# Revit family: Haworth_ComposeStorage_StorageUnit
name_source: partatom
category: Furniture Systems
revit_build: Autodesk Revit 2018 (Build: 20170223_1515(x64)
units: mm (PartAtom-declared; Revit-internal decimal feet)

## family parameters
Always vertical = Yes
Cut with Voids When Loaded = No
OmniClass Number = 23.40.70.14.64.21
OmniClass Title = Systems Furniture
Part Type = Normal
Room Calculation Point = No
Round Connector Dimension = Use Diameter
Shared = No
Work Plane-Based = No

## types (24) — shared parameters
Assembly Code = E2020200
Back Finish = Haworth _ Wood _ White Oak
Base = Yes
Base Finish = Haworth _ Wood _ White Oak
Base Height = 1"
Cabinet Finish = Haworth _ Wood _ White Oak
Chamfer Legs = No
Custom Size = No
Description = Haworth - Compose - Storage Unit
Door Finish = Haworth _ Wood _ White Oak
Finished Back = No
Manufacturer = Haworth
Max. Depth = 22"
Max. Height = 55"
Max. Width = 36"
Min. Depth = 16"
Min. Height = 19"
Min. Width = 30"
Model = BZS
Plynth Base = No
Revision Number = 4
Side Panel Base = Yes
Size = Verify Final Dim. w/ Haworth
Spacer Finish = Haworth _ Wood _ White Oak
Spacer Height = 0"
Standard Depths = 16, 22 in.
Standard Height = 14 1/4, 26 1/4, 38 1/4 in.
Standard Widths = 30, 36 in.
Sustainability Info = http://media.haworth.com
Top Spacer = No
URL = www.haworth.com
URL - Product = http://www.haworth.com
Warranty = http://www.haworth.com

## per-type parameters (varying)
| type | Actual Depth | Actual Height | Actual Width | Depth | Depth Adjuster | Door Height | Door Width | Doors | One High | Shelf 1 | Shelf 1 Offset | Shelf 2 | Shelf 2 Offet | Three High | Two High | Width |
| 1 High 30w 16d - No Doors | 16" | 14 1/4" | 30" | 16" | 0" | 13 1/4" | 15" | No | Yes | No | 4 43/256" | No | 4 43/256" | No | No | 30" |
| 1 High 30w 22d - No Doors | 22" | 14 1/4" | 30" | 22" | 0" | 13 1/4" | 15" | No | Yes | No | 4 43/256" | No | 4 43/256" | No | No | 30" |
| 1 High 36w 16d - No Doors | 16" | 14 1/4" | 36" | 16" | 0" | 13 1/4" | 18" | No | Yes | No | 4 43/256" | No | 4 43/256" | No | No | 36" |
| 1 High 36w 22d - No Doors | 22" | 14 1/4" | 36" | 22" | 0" | 13 1/4" | 18" | No | Yes | No | 4 43/256" | No | 4 43/256" | No | No | 36" |
| 2 High 30w 16d - No Doors | 16" | 26 1/4" | 30" | 16" | 0" | 25 1/4" | 15" | No | No | Yes | 12 5/8" | No | 8 43/256" | No | Yes | 30" |
| 2 High 30w 22d - No Doors | 22" | 26 1/4" | 30" | 22" | 0" | 25 1/4" | 15" | No | No | Yes | 12 5/8" | No | 8 43/256" | No | Yes | 30" |
| 2 High 36w 16d - No Doors | 16" | 26 1/4" | 36" | 16" | 0" | 25 1/4" | 18" | No | No | Yes | 12 5/8" | No | 8 43/256" | No | Yes | 36" |
| 2 High 36w 22d - No Doors | 22" | 26 1/4" | 36" | 22" | 0" | 25 1/4" | 18" | No | No | Yes | 12 5/8" | No | 8 43/256" | No | Yes | 36" |
| 3 High 30w 16d - No Doors | 16" | 38 1/4" | 30" | 16" | 0" | 37 1/4" | 15" | No | No | Yes | 12 43/256" | Yes | 12 43/256" | Yes | No | 30" |
| 3 High 30w 22d - No Doors | 22" | 38 1/4" | 30" | 22" | 0" | 37 1/4" | 15" | No | No | Yes | 12 43/256" | Yes | 12 43/256" | Yes | No | 30" |
| 3 High 36w 16d - No Doors | 16" | 38 1/4" | 36" | 16" | 0" | 37 1/4" | 18" | No | No | Yes | 12 43/256" | Yes | 12 43/256" | Yes | No | 36" |
| 3 High 36w 22d - No Doors | 22" | 38 1/4" | 36" | 22" | 0" | 37 1/4" | 18" | No | No | Yes | 12 43/256" | Yes | 12 43/256" | Yes | No | 36" |
| 1 High 30w 16d - With Doors | 17" | 14 1/4" | 30" | 16" | 1" | 13 1/4" | 15" | Yes | Yes | No | 4 43/256" | No | 4 43/256" | No | No | 30" |
| 1 High 30w 22d - With Doors | 23" | 14 1/4" | 30" | 22" | 1" | 13 1/4" | 15" | Yes | Yes | No | 4 43/256" | No | 4 43/256" | No | No | 30" |
| 1 High 36w 16d - With Doors | 17" | 14 1/4" | 36" | 16" | 1" | 13 1/4" | 18" | Yes | Yes | No | 4 43/256" | No | 4 43/256" | No | No | 36" |
| 1 High 36w 22d - With Doors | 23" | 14 1/4" | 36" | 22" | 1" | 13 1/4" | 18" | Yes | Yes | No | 4 43/256" | No | 4 43/256" | No | No | 36" |
| 2 High 30w 16d - With Doors | 17" | 26 1/4" | 30" | 16" | 1" | 25 1/4" | 15" | Yes | No | Yes | 12 5/8" | No | 8 43/256" | No | Yes | 30" |
| 2 High 30w 22d - With Doors | 23" | 26 1/4" | 30" | 22" | 1" | 25 1/4" | 15" | Yes | No | Yes | 12 5/8" | No | 8 43/256" | No | Yes | 30" |
| 2 High 36w 16d - With Doors | 17" | 26 1/4" | 36" | 16" | 1" | 25 1/4" | 18" | Yes | No | Yes | 12 5/8" | No | 8 43/256" | No | Yes | 36" |
| 2 High 36w 22d - With Doors | 23" | 26 1/4" | 36" | 22" | 1" | 25 1/4" | 18" | Yes | No | Yes | 12 5/8" | No | 8 43/256" | No | Yes | 36" |
| 3 High 30w 16d - With Doors | 17" | 38 1/4" | 30" | 16" | 1" | 37 1/4" | 15" | Yes | No | Yes | 12 43/256" | Yes | 12 43/256" | Yes | No | 30" |
| 3 High 30w 22d - With Doors | 23" | 38 1/4" | 30" | 22" | 1" | 37 1/4" | 15" | Yes | No | Yes | 12 43/256" | Yes | 12 43/256" | Yes | No | 30" |
| 3 High 36w 16d - With Doors | 17" | 38 1/4" | 36" | 16" | 1" | 37 1/4" | 18" | Yes | No | Yes | 12 43/256" | Yes | 12 43/256" | Yes | No | 36" |
| 3 High 36w 22d - With Doors | 23" | 38 1/4" | 36" | 22" | 1" | 37 1/4" | 18" | Yes | No | Yes | 12 43/256" | Yes | 12 43/256" | Yes | No | 36" |

## geometry (parser evidence)
native form markers: Sweep x14
no freeform markers — native parametric forms only
